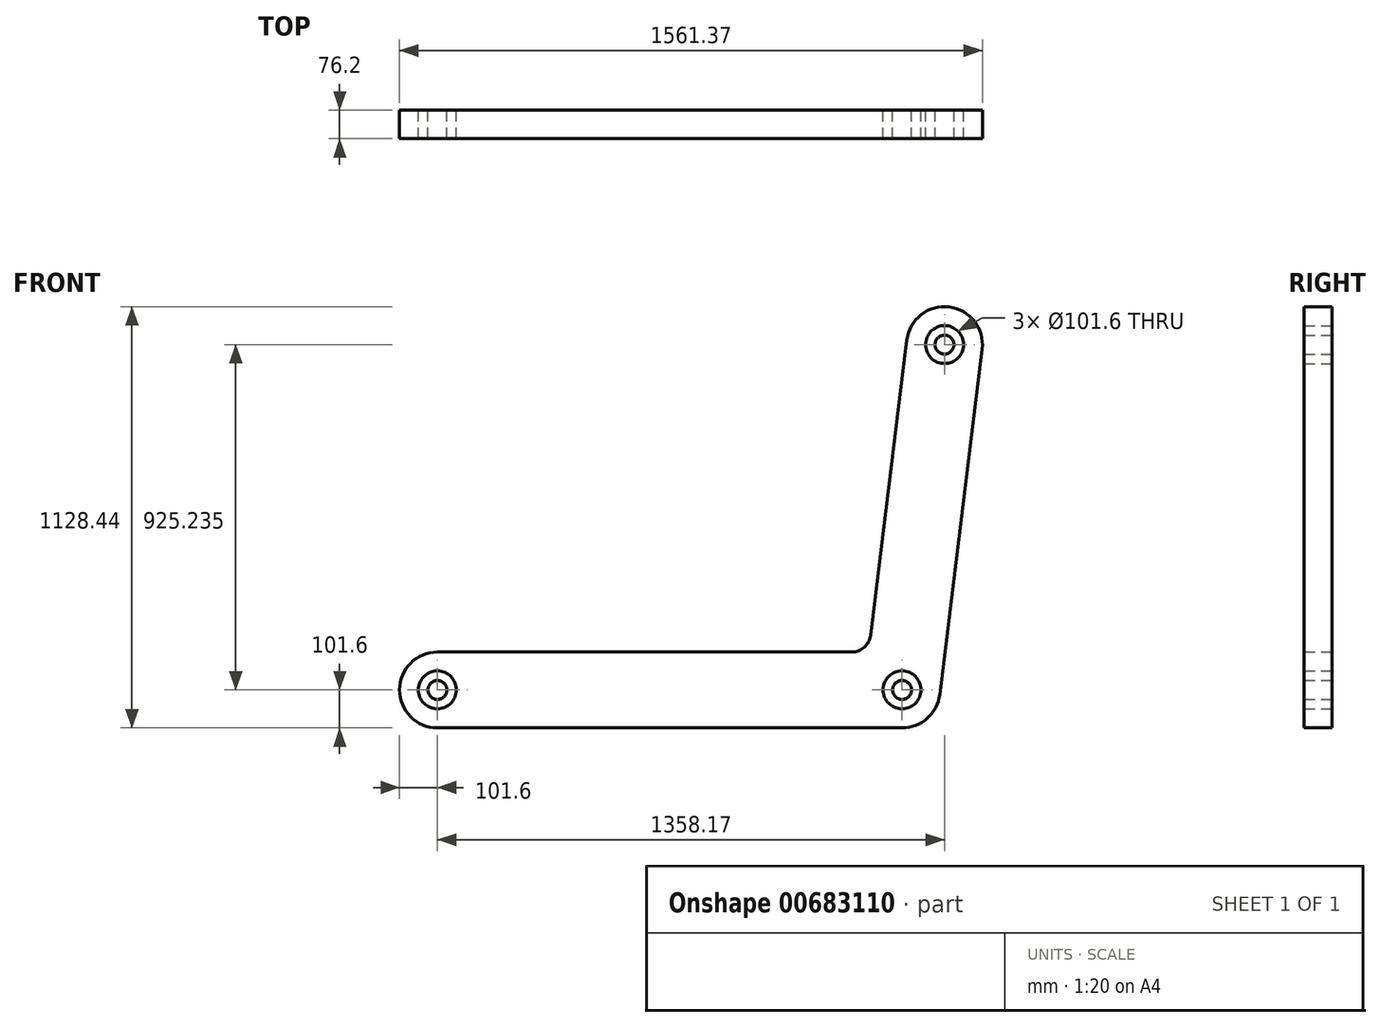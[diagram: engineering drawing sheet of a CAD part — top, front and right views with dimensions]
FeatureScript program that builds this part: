
annotation { "Feature Type Name" : "Feature", "Feature Type Description" : "" }
export const myFeature = defineFeature(function(context is Context, id is Id, definition is map)
    precondition{}
    {
        {
            var Q0;
            Q0=qCreatedBy(makeId("Front.planeOp"),FACE);
            var sketch = newSketch(context, id + "F0", { "sketchPlane" : qUnion([Q0])});
            skLineSegment(sketch, "E0", {"start": v(0, 0) * mm, "end": v(1244.6, 0) * mm});
            skLineSegment(sketch, "E1", {"start": v(1244.6, 0) * mm, "end": v(1358.17, 925.24) * mm});
            skLineSegment(sketch, "E2", {"start": v(1358.17, 925.24) * mm, "end": v(0, 0) * mm});
            skArc(sketch, "E3", {"start": v(0, 101.6) * mm, "mid": v(-101.6, 0) * mm, "end": v(0, -101.6) * mm});
            skArc(sketch, "E4", {"start": v(1244.6, -101.6) * mm, "mid": v(1311.92, -76.1) * mm, "end": v(1345.44, -12.38) * mm});
            skArc(sketch, "E5", {"start": v(1459.02, 912.86) * mm, "mid": v(1370.55, 1026.08) * mm, "end": v(1257.33, 937.61) * mm});
            skLineSegment(sketch, "E6.0", {"start": v(1345.44, -12.38) * mm, "end": v(1459.02, 912.86) * mm});
            skLineSegment(sketch, "E7.0", {"start": v(1160.19, 146.21) * mm, "end": v(1257.33, 937.61) * mm});
            skLineSegment(sketch, "E8.0", {"start": v(0, -101.6) * mm, "end": v(1244.6, -101.6) * mm});
            skLineSegment(sketch, "E9.0", {"start": v(0, 101.6) * mm, "end": v(1109.76, 101.6) * mm});
            skArc(sketch, "E10.filletArc", {"start": v(1109.76, 101.6) * mm, "mid": v(1143.43, 114.35) * mm, "end": v(1160.19, 146.21) * mm});
            skCircle(sketch, "E11", {"center": v(0, 0) * mm, "radius": 50.8 * mm});
            skCircle(sketch, "E12", {"center": v(1358.17, 925.24) * mm, "radius": 50.8 * mm});
            skCircle(sketch, "E13", {"center": v(1244.6, 0) * mm, "radius": 50.8 * mm});
            skCircle(sketch, "E14", {"center": v(0, 0) * mm, "radius": 25.4 * mm});
            skCircle(sketch, "E15", {"center": v(1244.6, 0) * mm, "radius": 25.4 * mm});
            skCircle(sketch, "E16", {"center": v(1358.17, 925.24) * mm, "radius": 25.4 * mm});
            skSolve(sketch);
        }
        {
            var Q0;
            {var subQ4=sQuery(id+"F0.wireOp",EDGE,"E3");Q0=makeQuery(id+"F0.imprint","IMPRINT",FACE,{"disambiguationData":[TD([[makeQuery(id+"F0.imprint","IMPRINT",EDGE,{"derivedFrom":subQ4}),1.0]])]});}
            var Q1;
            {var subQ9=sQuery(id+"F0.wireOp",EDGE,"E10.filletArc");Q1=makeQuery(id+"F0.imprint","IMPRINT",FACE,{"disambiguationData":[TD([[makeQuery(id+"F0.imprint","IMPRINT",EDGE,{"derivedFrom":subQ9}),-1.0]])]});}
            var Q2;
            {var subQ0=sQuery(id+"F0.wireOp",EDGE,"E2");var subQ1=sQuery(id+"F0.wireOp",EDGE,"E0");var subQ2=makeQuery(id+"F0.imprint","INTERSECT",VERTEX,{"derivedFrom":[subQ1,subQ0]});Q2=makeQuery(id+"F0.imprint","IMPRINT",FACE,{"disambiguationData":[TD([[makeQuery(id+"F0.imprint","IMPRINT",EDGE,{"disambiguationData":[TD([[subQ2,-1.0]])],"derivedFrom":subQ1}),-1.0]])]});}
            var Q3;
            {var subQ0=sQuery(id+"F0.wireOp",EDGE,"E1");var subQ1=sQuery(id+"F0.wireOp",EDGE,"E0");var subQ2=makeQuery(id+"F0.imprint","INTERSECT",VERTEX,{"derivedFrom":[subQ1,subQ0]});Q3=makeQuery(id+"F0.imprint","IMPRINT",FACE,{"disambiguationData":[TD([[makeQuery(id+"F0.imprint","IMPRINT",EDGE,{"disambiguationData":[TD([[subQ2,1.0]])],"derivedFrom":subQ1}),-1.0]])]});}
            var Q4;
            {var subQ0=sQuery(id+"F0.wireOp",EDGE,"E2");var subQ1=sQuery(id+"F0.wireOp",EDGE,"E1");var subQ2=makeQuery(id+"F0.imprint","INTERSECT",VERTEX,{"derivedFrom":[subQ1,subQ0]});Q4=makeQuery(id+"F0.imprint","IMPRINT",FACE,{"disambiguationData":[TD([[makeQuery(id+"F0.imprint","IMPRINT",EDGE,{"disambiguationData":[TD([[subQ2,1.0]])],"derivedFrom":subQ1}),-1.0]])]});}
            var Q5;
            {var subQ0=sQuery(id+"F0.wireOp",EDGE,"E2");var subQ1=sQuery(id+"F0.wireOp",EDGE,"E1");var subQ2=makeQuery(id+"F0.imprint","INTERSECT",VERTEX,{"derivedFrom":[subQ1,subQ0]});Q5=makeQuery(id+"F0.imprint","IMPRINT",FACE,{"disambiguationData":[TD([[makeQuery(id+"F0.imprint","IMPRINT",EDGE,{"disambiguationData":[TD([[subQ2,1.0]])],"derivedFrom":subQ1}),1.0]])]});}
            var Q6;
            {var subQ0=sQuery(id+"F0.wireOp",EDGE,"E1");var subQ1=sQuery(id+"F0.wireOp",EDGE,"E0");var subQ2=makeQuery(id+"F0.imprint","INTERSECT",VERTEX,{"derivedFrom":[subQ1,subQ0]});Q6=makeQuery(id+"F0.imprint","IMPRINT",FACE,{"disambiguationData":[TD([[makeQuery(id+"F0.imprint","IMPRINT",EDGE,{"disambiguationData":[TD([[subQ2,1.0]])],"derivedFrom":subQ1}),1.0]])]});}
            var Q7;
            {var subQ0=sQuery(id+"F0.wireOp",EDGE,"E2");var subQ1=sQuery(id+"F0.wireOp",EDGE,"E0");var subQ2=makeQuery(id+"F0.imprint","INTERSECT",VERTEX,{"derivedFrom":[subQ1,subQ0]});Q7=makeQuery(id+"F0.imprint","IMPRINT",FACE,{"disambiguationData":[TD([[makeQuery(id+"F0.imprint","IMPRINT",EDGE,{"disambiguationData":[TD([[subQ2,-1.0]])],"derivedFrom":subQ1}),1.0]])]});}
            extrude(context, id + "F1", {"entities" : qUnion([Q0, Q1, Q2, Q3, Q4, Q5, Q6, Q7]), "depth" : 76.2 * mm, "offsetDistance" : 25.4 * mm});
        }
    });
